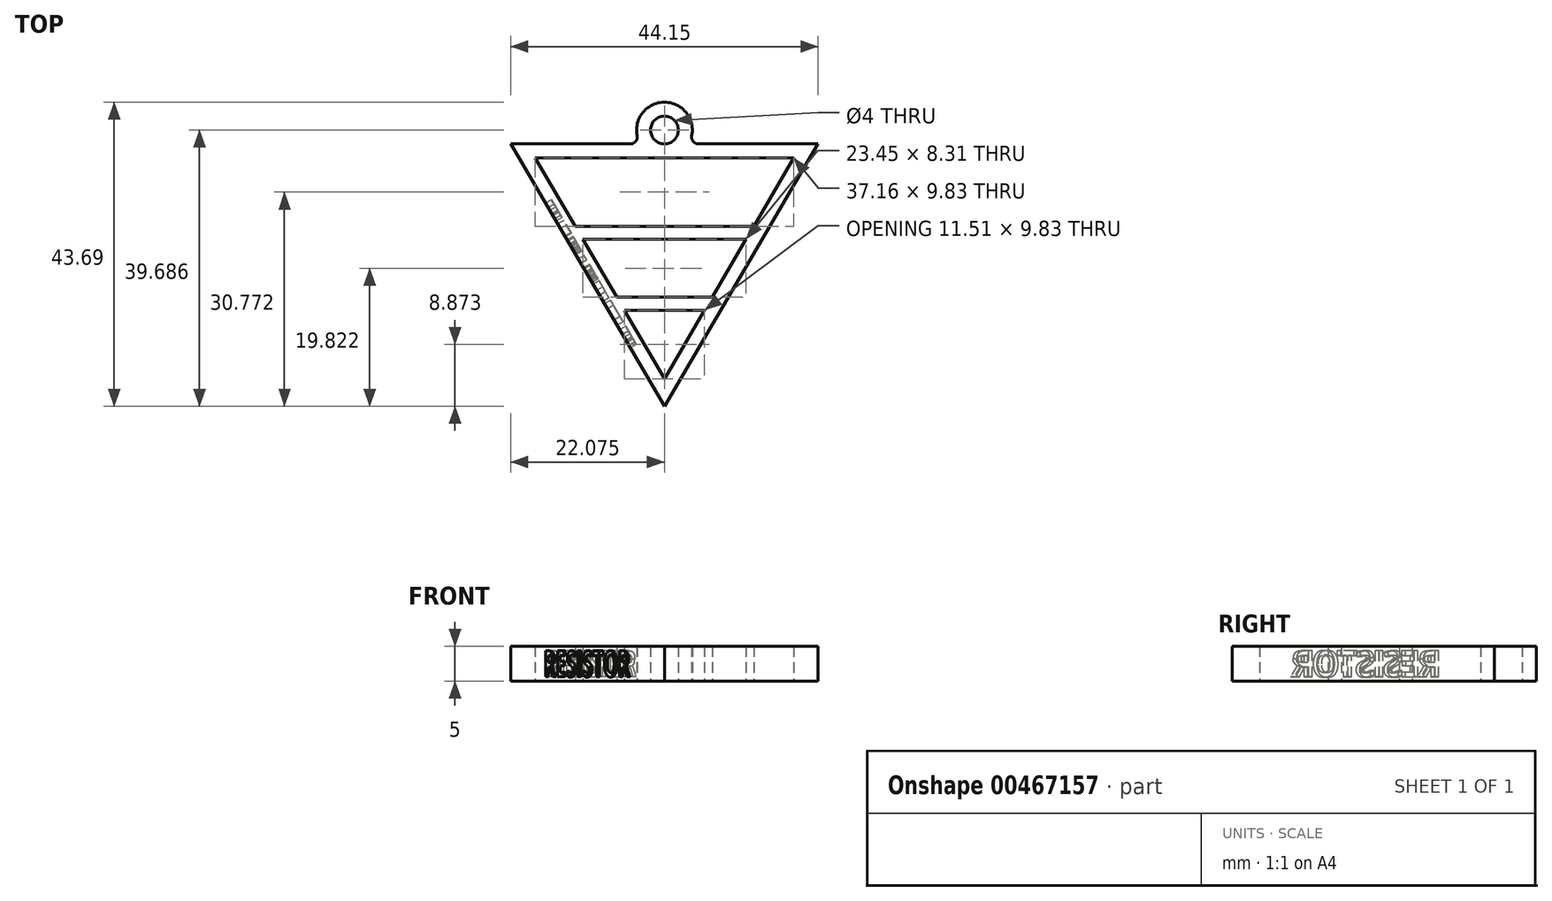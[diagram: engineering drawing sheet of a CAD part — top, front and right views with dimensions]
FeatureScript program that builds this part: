
annotation { "Feature Type Name" : "Feature", "Feature Type Description" : "" }
export const myFeature = defineFeature(function(context is Context, id is Id, definition is map)
    precondition{}
    {
        {
            var Q0;
            Q0=qCreatedBy(makeId("Top.planeOp"),FACE);
            var sketch = newSketch(context, id + "F0", { "sketchPlane" : qUnion([Q0])});
            skLineSegment(sketch, "E0", {"start": v(-9.18, 12.02) * mm, "end": v(9.4, 12.02) * mm});
            skLineSegment(sketch, "E1", {"start": v(27.99, 12.02) * mm, "end": v(22.23, 2.19) * mm});
            skLineSegment(sketch, "E2", {"start": v(9.4, -19.71) * mm, "end": v(3.65, -9.88) * mm});
            skLineSegment(sketch, "E3", {"start": v(9.4, -19.71) * mm, "end": v(9.4, -9.88) * mm, "construction": true});
            skLineSegment(sketch, "E4", {"start": v(2.55, -8) * mm, "end": v(9.4, -8) * mm});
            skLineSegment(sketch, "E5", {"start": v(3.65, -9.88) * mm, "end": v(9.4, -9.88) * mm});
            skLineSegment(sketch, "E6", {"start": v(-3.42, 2.19) * mm, "end": v(-9.18, 12.02) * mm});
            skLineSegment(sketch, "E7", {"start": v(-2.32, 0.3) * mm, "end": v(-3.42, 2.19) * mm, "construction": true});
            skLineSegment(sketch, "E8", {"start": v(2.55, -8) * mm, "end": v(-2.32, 0.3) * mm});
            skLineSegment(sketch, "E9", {"start": v(3.65, -9.88) * mm, "end": v(2.55, -8) * mm, "construction": true});
            skLineSegment(sketch, "E10", {"start": v(15.16, -9.88) * mm, "end": v(9.4, -19.71) * mm});
            skLineSegment(sketch, "E11", {"start": v(16.26, -8) * mm, "end": v(15.16, -9.88) * mm, "construction": true});
            skLineSegment(sketch, "E12", {"start": v(21.13, 0.3) * mm, "end": v(16.26, -8) * mm});
            skLineSegment(sketch, "E13", {"start": v(22.23, 2.19) * mm, "end": v(21.13, 0.3) * mm, "construction": true});
            skLineSegment(sketch, "E14", {"start": v(9.4, 12.02) * mm, "end": v(27.99, 12.02) * mm});
            skLineSegment(sketch, "E15", {"start": v(9.4, -8) * mm, "end": v(16.26, -8) * mm});
            skLineSegment(sketch, "E16", {"start": v(9.4, -9.88) * mm, "end": v(15.16, -9.88) * mm});
            skLineSegment(sketch, "E17", {"start": v(9.4, 2.19) * mm, "end": v(22.23, 2.19) * mm});
            skLineSegment(sketch, "E18", {"start": v(9.4, 2.19) * mm, "end": v(9.4, 12.02) * mm, "construction": true});
            skLineSegment(sketch, "E19", {"start": v(9.4, 2.19) * mm, "end": v(-3.42, 2.19) * mm});
            skLineSegment(sketch, "E20", {"start": v(-2.32, 0.3) * mm, "end": v(9.4, 0.3) * mm});
            skLineSegment(sketch, "E21", {"start": v(9.4, 0.3) * mm, "end": v(21.13, 0.3) * mm});
            skLineSegment(sketch, "E22", {"start": v(9.4, 2.19) * mm, "end": v(9.4, 0.3) * mm, "construction": true});
            skLineSegment(sketch, "E23", {"start": v(9.4, -9.88) * mm, "end": v(9.4, -8) * mm, "construction": true});
            skLineSegment(sketch, "E24", {"start": v(9.4, 0.3) * mm, "end": v(9.4, -8) * mm, "construction": true});
            skLineSegment(sketch, "E25", {"start": v(9.4, -23.67) * mm, "end": v(-12.67, 14.02) * mm});
            skLineSegment(sketch, "E26", {"start": v(-12.67, 14.02) * mm, "end": v(4.5, 14.02) * mm});
            skLineSegment(sketch, "E27", {"start": v(31.48, 14.02) * mm, "end": v(9.4, -23.67) * mm});
            skLineSegment(sketch, "E28", {"start": v(9.4, 12.02) * mm, "end": v(9.4, 14.02) * mm, "construction": true});
            skLineSegment(sketch, "E29", {"start": v(-2.32, 0.3) * mm, "end": v(-4.04, -0.7) * mm, "construction": true});
            skLineSegment(sketch, "E30", {"start": v(21.13, 0.3) * mm, "end": v(22.86, -0.7) * mm, "construction": true});
            skPoint(sketch, "E31.first.point", {"position": v(5.94, 14.02) * mm});
            skPoint(sketch, "E31.second.point", {"position": v(12.87, 14.02) * mm});
            skPoint(sketch, "E31.third.point", {"position": v(9.4, 20.02) * mm});
            skPoint(sketch, "E31.third.point.positionSnap0", {"position": v(9.4, 7.1) * mm});
            skCircle(sketch, "E32", {"center": v(9.4, 16.02) * mm, "radius": 2 * mm});
            skArc(sketch, "E33", {"start": v(5.94, 14.02) * mm, "mid": v(9.4, 12.02) * mm, "end": v(12.87, 14.02) * mm, "construction": true});
            skArc(sketch, "E34", {"start": v(13.32, 15.22) * mm, "mid": v(9.4, 20.02) * mm, "end": v(5.49, 15.22) * mm});
            skLineSegment(sketch, "E35", {"start": v(5.94, 14.02) * mm, "end": v(12.87, 14.02) * mm, "construction": true});
            skLineSegment(sketch, "E36", {"start": v(14.3, 14.02) * mm, "end": v(31.48, 14.02) * mm});
            skArc(sketch, "E37.filletArc", {"start": v(4.5, 14.02) * mm, "mid": v(5.28, 14.38) * mm, "end": v(5.49, 15.22) * mm});
            skArc(sketch, "E38.filletArc", {"start": v(13.32, 15.22) * mm, "mid": v(13.53, 14.38) * mm, "end": v(14.3, 14.02) * mm});
            skSolve(sketch);
        }
        {
            var Q0;
            Q0 = qSketchRegion(id + "F0", true);
            extrude(context, id + "F1", {"entities" : qUnion([Q0]), "endBound" : BoundingType.SYMMETRIC, "depth" : 5 * mm});
        }
        {
            var Q0;
            Q0=makeQuery(id+"F1.opExtrude","SWEPT_FACE",FACE,{"disambiguationData":[OSD([sQuery(id+"F0.wireOp",EDGE,"E25")])]});
            var sketch = newSketch(context, id + "F2", { "sketchPlane" : qUnion([Q0])});
            skText(sketch, "E39", { "text": "RESISTOR", "fontName": "OpenSans-Bold.ttf"});
            skLineSegment(sketch, "E40", {"start": v(-5.33, 1.89) * mm, "end": v(-5.33, 2.5) * mm, "construction": true});
            skLineSegment(sketch, "E41", {"start": v(-5.33, -1.89) * mm, "end": v(-5.33, -2.5) * mm, "construction": true});
            skLineSegment(sketch, "E42", {"start": v(-18.5, 0) * mm, "end": v(-9.1, 0) * mm, "construction": true});
            skLineSegment(sketch, "E43", {"start": v(15.79, 0) * mm, "end": v(25.18, 0) * mm, "construction": true});
            const initialGuessF2  = {"E39": [-0.0091, -0.00189, 1, 0, 0.00377]};
            skSetInitialGuess(sketch, initialGuessF2);
            skSolve(sketch);
        }
        {
            var Q0;
            Q0 = qSketchRegion(id + "F2", true);
            extrude(context, id + "F3", {"entities" : qUnion([Q0]), "operationType" : NewBodyOperationType.REMOVE, "oppositeDirection" : true, "depth" : 1 * mm});
        }
    });
